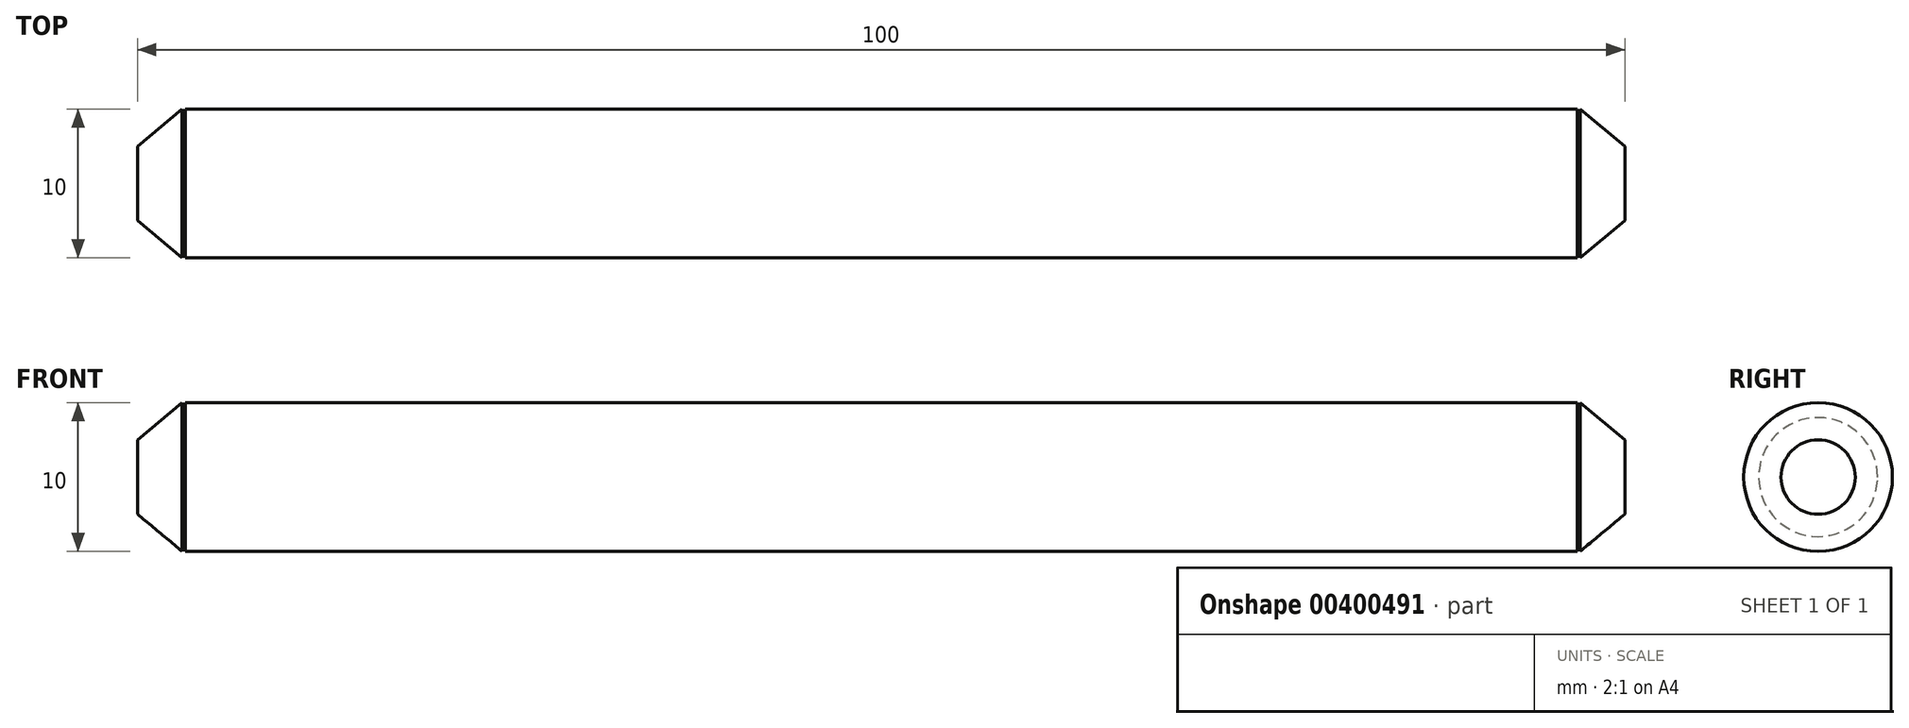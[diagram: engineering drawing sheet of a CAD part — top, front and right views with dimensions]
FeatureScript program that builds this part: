
annotation { "Feature Type Name" : "Feature", "Feature Type Description" : "" }
export const myFeature = defineFeature(function(context is Context, id is Id, definition is map)
    precondition{}
    {
        {
            var Q0;
            Q0=qCreatedBy(makeId("Front.planeOp"),FACE);
            var sketch = newSketch(context, id + "F0", { "sketchPlane" : qUnion([Q0])});
            skLineSegment(sketch, "E0.bottom", {"start": v(0, 0) * mm, "end": v(-100, 0) * mm});
            skLineSegment(sketch, "E0.top", {"start": v(-3.2, 5) * mm, "end": v(-96.8, 5) * mm});
            skLineSegment(sketch, "E0.left", {"start": v(0, 0) * mm, "end": v(0, 2.5) * mm});
            skLineSegment(sketch, "E0.right", {"start": v(-100, 0) * mm, "end": v(-100, 2.5) * mm});
            skLineSegment(sketch, "E1", {"start": v(0, 2.5) * mm, "end": v(-3, 5) * mm});
            skLineSegment(sketch, "E2", {"start": v(-100, 2.5) * mm, "end": v(-97, 5) * mm});
            skLineSegment(sketch, "E3.top", {"start": v(-97, 4) * mm, "end": v(-96.8, 4) * mm});
            skLineSegment(sketch, "E3.left", {"start": v(-97, 5) * mm, "end": v(-97, 4) * mm});
            skLineSegment(sketch, "E3.right", {"start": v(-96.8, 5) * mm, "end": v(-96.8, 4) * mm});
            skLineSegment(sketch, "E4.top", {"start": v(-3, 4) * mm, "end": v(-3.2, 4) * mm});
            skLineSegment(sketch, "E4.left", {"start": v(-3, 5) * mm, "end": v(-3, 4) * mm});
            skLineSegment(sketch, "E4.right", {"start": v(-3.2, 5) * mm, "end": v(-3.2, 4) * mm});
            skSolve(sketch);
        }
        {
            var Q0;
            Q0 = qSketchRegion(id + "F0", true);
            var Q1;
            Q1=sQuery(id+"F0.wireOp",EDGE,"E0.bottom");
            revolve(context, id + "F1", {"entities" : qUnion([Q0]), "axis" : qUnion([Q1]), "revolveType" : RevolveType.FULL});
        }
    });
